# Revit family: Symetra_Straight_Final
name_source: partatom
category: Furniture
revit_build: Autodesk Revit Architecture 2014 (Build: 20131024_2115(x64)
units: mm (PartAtom-declared; Revit-internal decimal feet)

## types (1)
- Symetra_Straight_Final
    Actual Depth = 2' - 0"
    Assembly Code = E2010
    Description = Lecture hall tables
    End Panel Depth = 1' - 10"
    Leg Finish = Leg Finish
    Leg Set Back = 0' - 7"
    Manufacturer = Navetta
    Max Depth = 2' - 6"
    Min Depth = 1' - 6"
    Min. Table Length = 60in.
    Model = Symetra
    Modesty & End Panel Finish = <By Category>
    Modesty Panel  Laminate = Yes
    Modesty Panel  Steel = No
    Modesty Panel 12"H = Yes
    Modesty Panel 14"H = No
    Modesty Panel 26"H = No
    Modesty Panel Actual Height = 1' - 0"
    Power Depth = 1' - 1 11/32"
    Power Finish = <By Category>
    Standard Modesty Panel Heights = 12,14,26 in.
    Standard Table Depths = 18-30 in.
    Table Depth = 2' - 0"
    Table Height = 2' - 5"
    Table Top Finish = <By Category>
    URL = http://navettadesign.com
    Version = 1

## geometry (parser evidence)
native form markers: Blend x4, Sweep x30
no freeform markers — native parametric forms only
